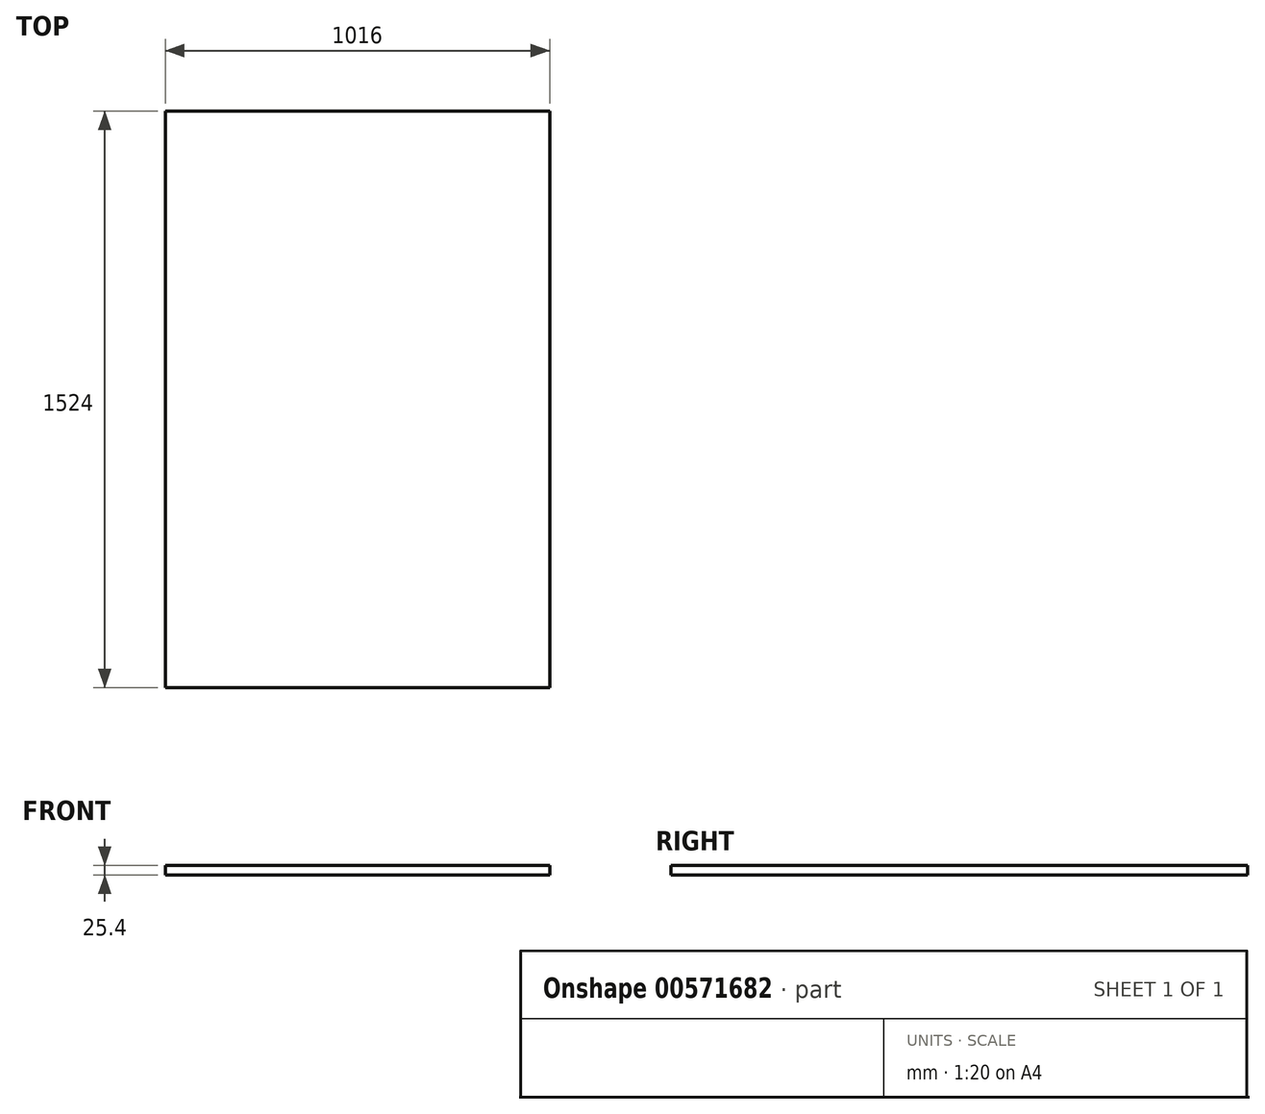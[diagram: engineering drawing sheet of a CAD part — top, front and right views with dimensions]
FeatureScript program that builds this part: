
annotation { "Feature Type Name" : "Feature", "Feature Type Description" : "" }
export const myFeature = defineFeature(function(context is Context, id is Id, definition is map)
    precondition{}
    {
        {
            var Q0;
            Q0=qCreatedBy(makeId("Top.planeOp"),FACE);
            var sketch = newSketch(context, id + "F0", { "sketchPlane" : qUnion([Q0])});
            skLineSegment(sketch, "E0", {"start": v(0, 0) * mm, "end": v(1016, 0) * mm});
            skLineSegment(sketch, "E1", {"start": v(1016, 0) * mm, "end": v(0, 0) * mm});
            skLineSegment(sketch, "E2", {"start": v(0, 0) * mm, "end": v(0, 1524) * mm});
            skLineSegment(sketch, "E3", {"start": v(0, 1524) * mm, "end": v(1016, 1524) * mm});
            skLineSegment(sketch, "E4", {"start": v(1016, 0) * mm, "end": v(1016, 1524) * mm});
            skSolve(sketch);
        }
        {
            var Q0;
            Q0 = qSketchRegion(id + "F0", true);
            extrude(context, id + "F1", {"entities" : qUnion([Q0]), "depth" : 25.4 * mm, "offsetDistance" : 25.4 * mm});
        }
    });
